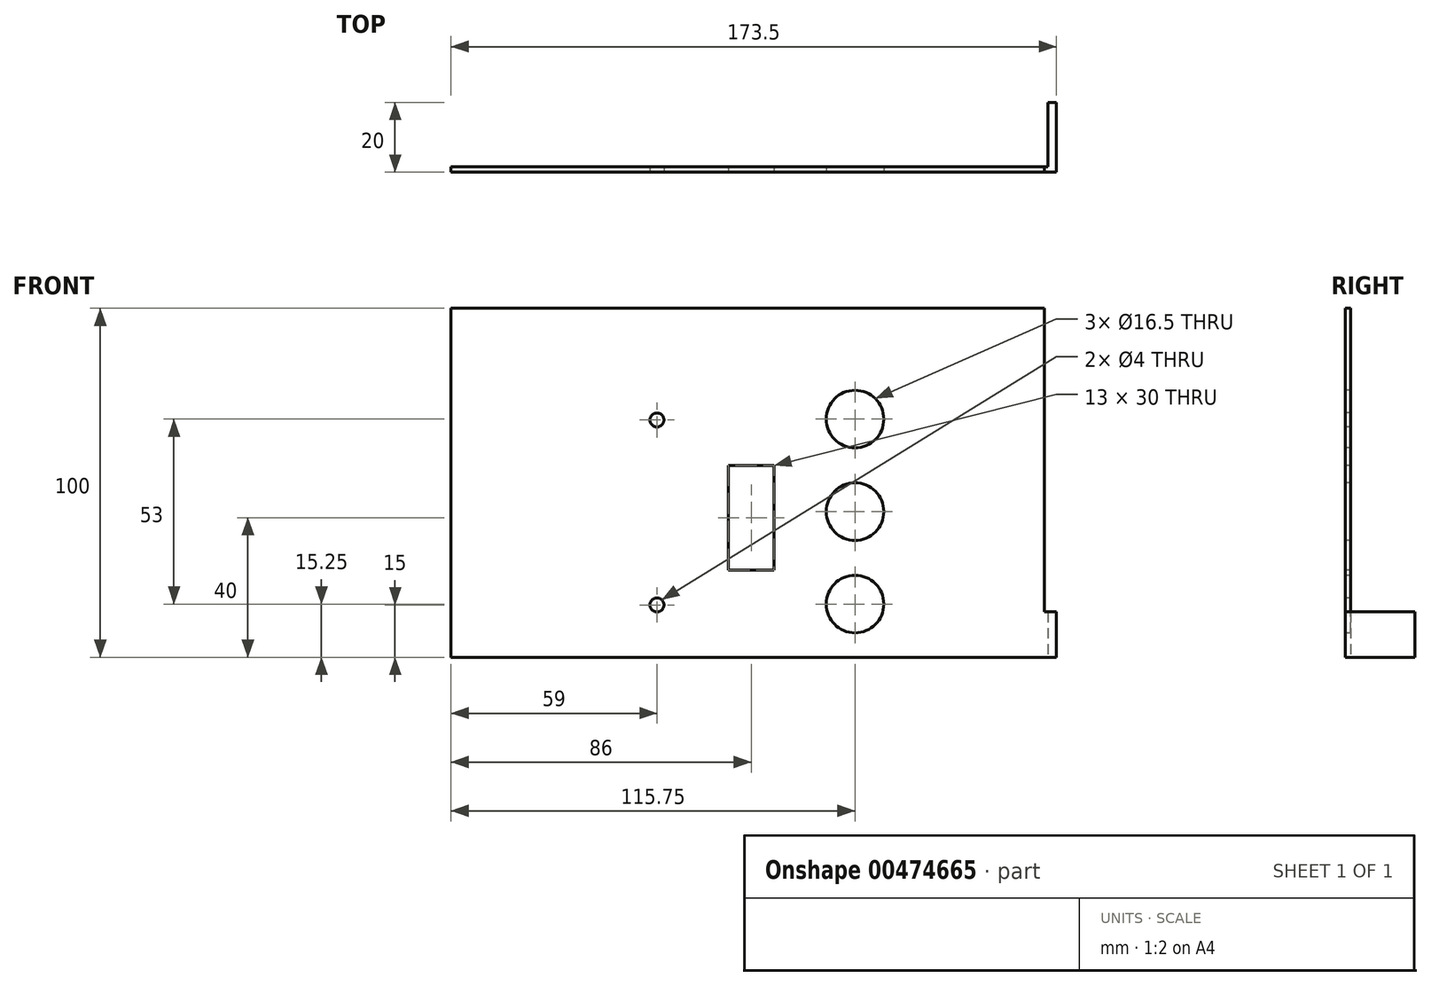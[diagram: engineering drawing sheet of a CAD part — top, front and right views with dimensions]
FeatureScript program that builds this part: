
annotation { "Feature Type Name" : "Feature", "Feature Type Description" : "" }
export const myFeature = defineFeature(function(context is Context, id is Id, definition is map)
    precondition{}
    {
        {
            var Q0;
            Q0=qCreatedBy(makeId("Front.planeOp"),FACE);
            var sketch = newSketch(context, id + "F0", { "sketchPlane" : qUnion([Q0])});
            skLineSegment(sketch, "E0.bottom", {"start": v(85, 50) * mm, "end": v(-85, 50) * mm});
            skLineSegment(sketch, "E0.top", {"start": v(85, -50) * mm, "end": v(-85, -50) * mm});
            skLineSegment(sketch, "E0.left", {"start": v(85, 50) * mm, "end": v(85, -50) * mm});
            skLineSegment(sketch, "E0.right", {"start": v(-85, 50) * mm, "end": v(-85, -50) * mm});
            skPoint(sketch, "E0.middle", {"position": v(0, 0) * mm});
            skSolve(sketch);
        }
        {
            var Q0;
            Q0=qSketchRegion(id+"F0",true);
            extrude(context, id + "F1", {"entities" : qUnion([Q0]), "depth" : 1.5 * mm, "offsetDistance" : 25 * mm});
        }
        {
            var Q0;
            Q0=makeQuery(id+"F1.opExtrude","CAP_FACE",FACE,{"disambiguationData":[OSD([sQuery(id+"F0.wireOp",EDGE,"E0.bottom"),sQuery(id+"F0.wireOp",EDGE,"E0.top"),sQuery(id+"F0.wireOp",EDGE,"E0.left"),sQuery(id+"F0.wireOp",EDGE,"E0.right")])],"isStart":false});
            var sketch = newSketch(context, id + "F2", { "sketchPlane" : qUnion([Q0])});
            skCircle(sketch, "E1", {"center": v(30.75, -34.75) * mm, "radius": 8.25 * mm});
            skCircle(sketch, "E2", {"center": v(30.75, -8.25) * mm, "radius": 8.25 * mm});
            skCircle(sketch, "E3", {"center": v(30.75, 18.25) * mm, "radius": 8.25 * mm});
            skLineSegment(sketch, "E4.bottom", {"start": v(7.5, -25) * mm, "end": v(-5.5, -25) * mm});
            skLineSegment(sketch, "E4.top", {"start": v(7.5, 5) * mm, "end": v(-5.5, 5) * mm});
            skLineSegment(sketch, "E4.left", {"start": v(7.5, -25) * mm, "end": v(7.5, 5) * mm});
            skLineSegment(sketch, "E4.right", {"start": v(-5.5, -25) * mm, "end": v(-5.5, 5) * mm});
            skPoint(sketch, "E4.middle", {"position": v(1, -10) * mm});
            skCircle(sketch, "E5", {"center": v(-26, -35) * mm, "radius": 2 * mm});
            skCircle(sketch, "E6", {"center": v(-26, 18) * mm, "radius": 2 * mm});
            skSolve(sketch);
        }
        {
            var Q0;
            Q0=qSketchRegion(id+"F2",true);
            extrude(context, id + "F3", {"entities" : qUnion([Q0]), "operationType" : NewBodyOperationType.REMOVE, "oppositeDirection" : true, "depth" : 25 * mm});
        }
        {
            var Q0;
            Q0=makeQuery(id+"F1.opExtrude","SWEPT_FACE",FACE,{"disambiguationData":[OSD([sQuery(id+"F0.wireOp",EDGE,"E0.left")])]});
            var sketch = newSketch(context, id + "F4", { "sketchPlane" : qUnion([Q0])});
            skLineSegment(sketch, "E7.bottom", {"start": v(-1.5, -50) * mm, "end": v(18.5, -50) * mm});
            skLineSegment(sketch, "E7.top", {"start": v(-1.5, -37) * mm, "end": v(18.5, -37) * mm});
            skLineSegment(sketch, "E7.left", {"start": v(-1.5, -50) * mm, "end": v(-1.5, -37) * mm});
            skLineSegment(sketch, "E7.right", {"start": v(18.5, -50) * mm, "end": v(18.5, -37) * mm});
            skSolve(sketch);
        }
        {
            var Q0;
            Q0 = qSketchRegion(id + "F4", true);
            extrude(context, id + "F5", {"entities" : qUnion([Q0]), "operationType" : NewBodyOperationType.ADD, "depth" : 3.5 * mm, "offsetDistance" : 25 * mm});
        }
        {
            var Q0;
            Q0=makeQuery(id+"F5.opExtrude","CAP_FACE",FACE,{"disambiguationData":[OSD([sQuery(id+"F4.wireOp",EDGE,"E7.bottom"),sQuery(id+"F4.wireOp",EDGE,"E7.top"),sQuery(id+"F4.wireOp",EDGE,"E7.left"),sQuery(id+"F4.wireOp",EDGE,"E7.right")])],"isStart":true});
            var sketch = newSketch(context, id + "F6", { "sketchPlane" : qUnion([Q0])});
            skLineSegment(sketch, "E8.0.0", {"start": v(0, -50) * mm, "end": v(0, -37) * mm});
            skLineSegment(sketch, "E8.0.1", {"start": v(0, -37) * mm, "end": v(-18.5, -37) * mm});
            skLineSegment(sketch, "E8.0.2", {"start": v(-18.5, -37) * mm, "end": v(-18.5, -50) * mm});
            skLineSegment(sketch, "E8.0.3", {"start": v(-18.5, -50) * mm, "end": v(0, -50) * mm});
            skSolve(sketch);
        }
        {
            var Q0;
            Q0 = qSketchRegion(id + "F6", true);
            extrude(context, id + "F7", {"entities" : qUnion([Q0]), "operationType" : NewBodyOperationType.REMOVE, "oppositeDirection" : true, "depth" : 1 * mm, "offsetDistance" : 25 * mm});
        }
    });
